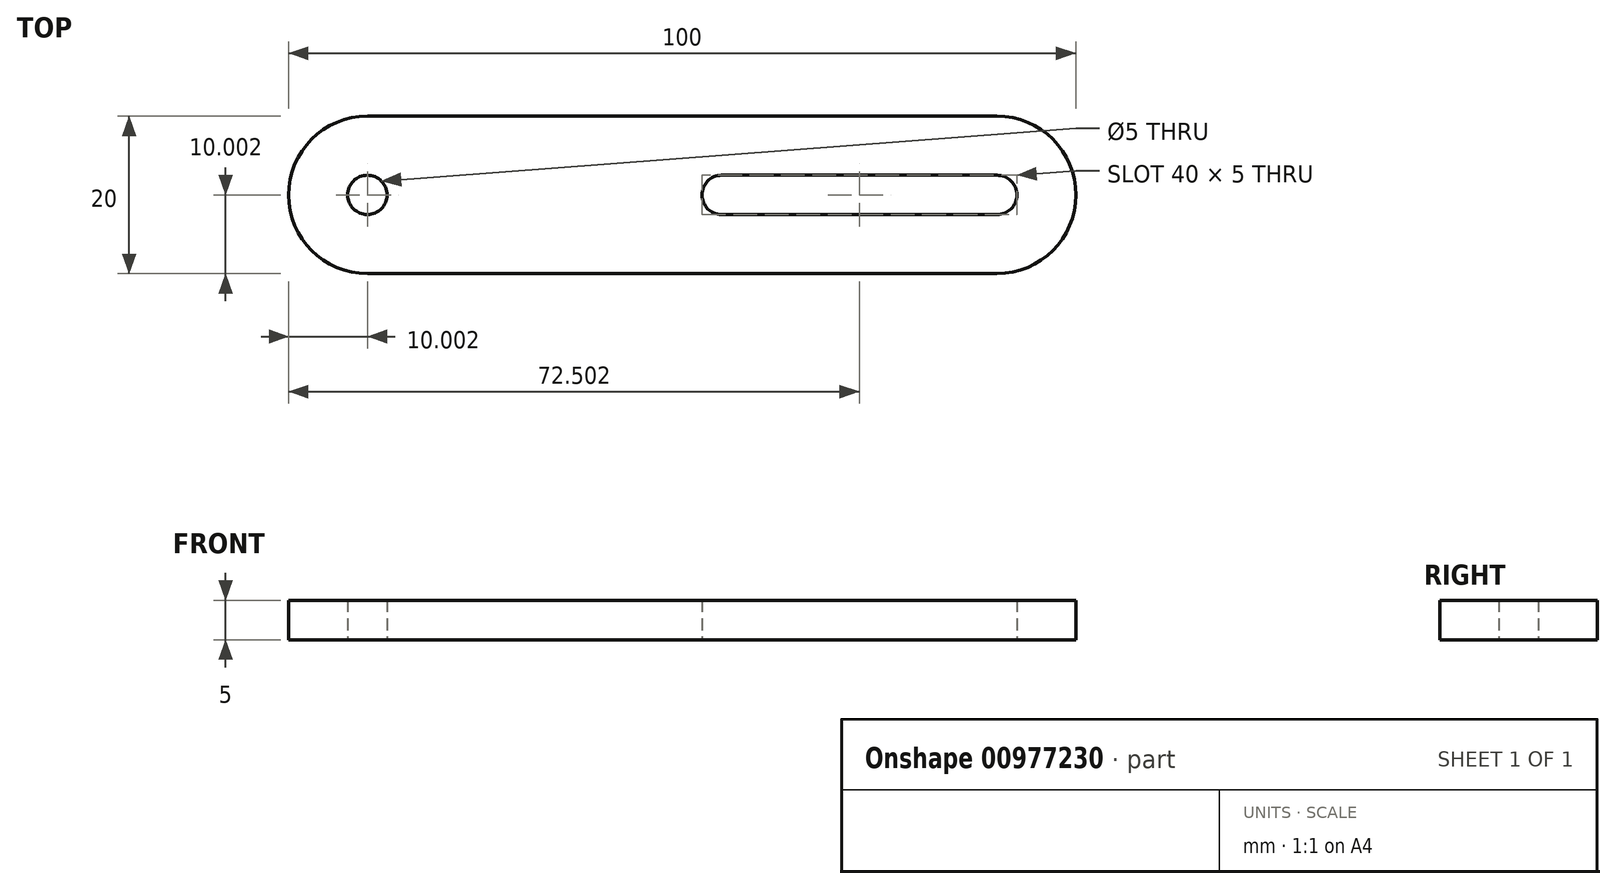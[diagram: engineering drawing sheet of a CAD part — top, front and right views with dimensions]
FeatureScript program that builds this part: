
annotation { "Feature Type Name" : "Feature", "Feature Type Description" : "" }
export const myFeature = defineFeature(function(context is Context, id is Id, definition is map)
    precondition{}
    {
        {
            var Q0;
            Q0=qCreatedBy(makeId("Top.planeOp"),FACE);
            var sketch = newSketch(context, id + "F0", { "sketchPlane" : qUnion([Q0])});
            skLineSegment(sketch, "E0.bottom", {"start": v(-37.64, 9.98) * mm, "end": v(42.36, 9.98) * mm});
            skLineSegment(sketch, "E0.top", {"start": v(-37.64, -10.02) * mm, "end": v(42.36, -10.02) * mm});
            skLineSegment(sketch, "E0.left", {"start": v(-47.64, -0.02) * mm, "end": v(-47.64, -0.02) * mm});
            skLineSegment(sketch, "E0.right", {"start": v(52.36, -0.02) * mm, "end": v(52.36, -0.02) * mm});
            skPoint(sketch, "E1.visualSharp", {"position": v(-47.64, 9.98) * mm});
            skArc(sketch, "E1.filletArc", {"start": v(-37.64, 9.98) * mm, "mid": v(-44.7, 7.05) * mm, "end": v(-47.64, -0.02) * mm});
            skPoint(sketch, "E2.visualSharp", {"position": v(52.36, 9.98) * mm});
            skArc(sketch, "E2.filletArc", {"start": v(52.36, -0.02) * mm, "mid": v(49.43, 7.05) * mm, "end": v(42.36, 9.98) * mm});
            skPoint(sketch, "E3.visualSharp", {"position": v(52.36, -10.02) * mm});
            skArc(sketch, "E3.filletArc", {"start": v(42.36, -10.02) * mm, "mid": v(49.43, -7.09) * mm, "end": v(52.36, -0.02) * mm});
            skPoint(sketch, "E4.visualSharp", {"position": v(-47.64, -10.02) * mm});
            skArc(sketch, "E4.filletArc", {"start": v(-47.64, -0.02) * mm, "mid": v(-44.7, -7.09) * mm, "end": v(-37.64, -10.02) * mm});
            skCircle(sketch, "E5", {"center": v(-37.64, -0.02) * mm, "radius": 2.5 * mm});
            skLineSegment(sketch, "E6.bottom", {"start": v(7.36, 2.48) * mm, "end": v(42.36, 2.48) * mm});
            skLineSegment(sketch, "E6.top", {"start": v(7.36, -2.52) * mm, "end": v(42.36, -2.52) * mm});
            skLineSegment(sketch, "E6.left", {"start": v(4.86, -0.02) * mm, "end": v(4.86, -0.02) * mm});
            skLineSegment(sketch, "E6.right", {"start": v(44.86, -0.02) * mm, "end": v(44.86, -0.02) * mm});
            skPoint(sketch, "E7.visualSharp", {"position": v(4.86, 2.48) * mm});
            skArc(sketch, "E7.filletArc", {"start": v(7.36, 2.48) * mm, "mid": v(5.6, 1.75) * mm, "end": v(4.86, -0.02) * mm});
            skPoint(sketch, "E8.visualSharp", {"position": v(44.86, 2.48) * mm});
            skArc(sketch, "E8.filletArc", {"start": v(44.86, -0.02) * mm, "mid": v(44.13, 1.75) * mm, "end": v(42.36, 2.48) * mm});
            skPoint(sketch, "E9.visualSharp", {"position": v(44.86, -2.52) * mm});
            skArc(sketch, "E9.filletArc", {"start": v(42.36, -2.52) * mm, "mid": v(44.13, -1.79) * mm, "end": v(44.86, -0.02) * mm});
            skPoint(sketch, "E10.visualSharp", {"position": v(4.86, -2.52) * mm});
            skArc(sketch, "E10.filletArc", {"start": v(4.86, -0.02) * mm, "mid": v(5.6, -1.79) * mm, "end": v(7.36, -2.52) * mm});
            skSolve(sketch);
        }
        {
            var Q0;
            Q0 = qSketchRegion(id + "F0", true);
            extrude(context, id + "F1", {"entities" : qUnion([Q0]), "depth" : 5 * mm, "offsetDistance" : 25 * mm});
        }
    });
